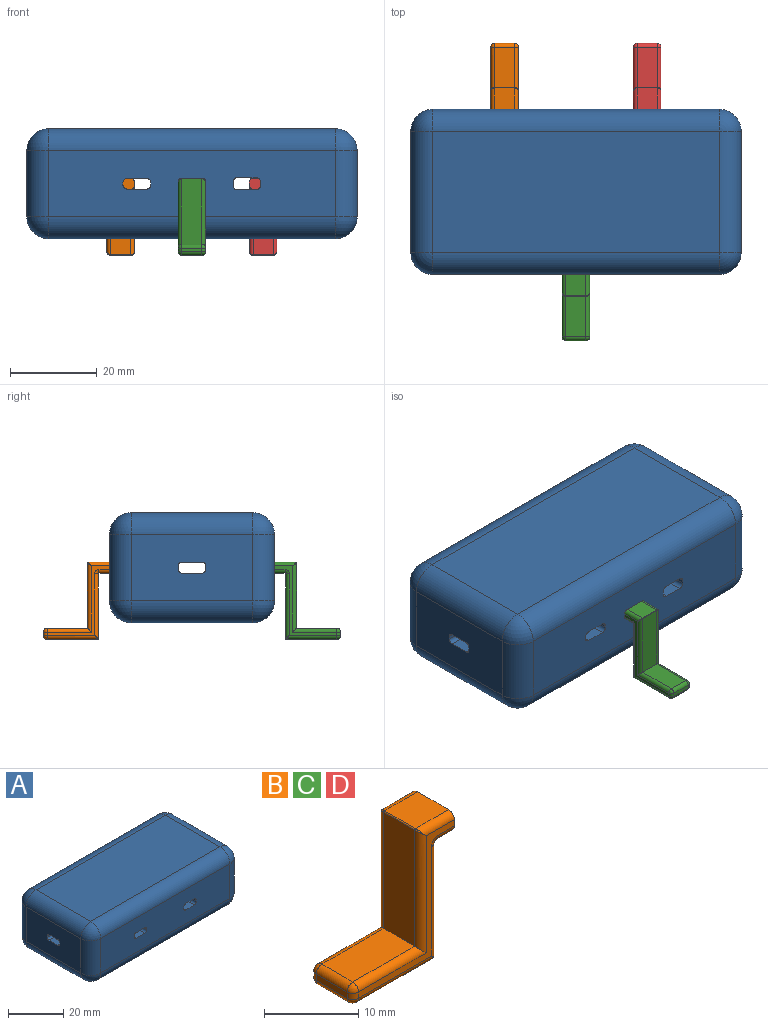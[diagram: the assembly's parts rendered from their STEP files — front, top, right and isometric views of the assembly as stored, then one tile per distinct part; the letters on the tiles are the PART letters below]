
ASSEMBLY  parts=4 mates=1
PART A: 70 faces, bbox 76.2x38.1x25.4 mm
  f0: plane 27.94x15.24mm, normal (1,0,0), area 410.4mm2, adj f21,f30,f31,f35,f62,f63,f64,f65
  f1: plane 27.94x15.24mm, normal (-1,0,0), area 410.4mm2, adj f16,f19,f23,f24,f52,f53,f54,f55
  f2: plane 15.88x0.41mm, normal (1,0,0), area 6.5mm2, adj f9,f12,f37,f60
  f3: cylinder r=1.02mm len=16.48mm, axis (0,1,0), area 25.7mm2, adj f4,f13,f36,f54,f61
  f4: plane 16.48x4.44mm, normal (0,0,-1), area 73.2mm2, adj f3,f5,f13,f54
  f5: cylinder r=1.02mm len=16.48mm, axis (0,1,0), area 25.7mm2, adj f4,f13,f40,f54,f59
  f6: plane 15.88x0.41mm, normal (-1,0,0), area 6.5mm2, adj f7,f12,f39,f58
  f7: cylinder r=1.02mm len=16.48mm, axis (0,1,0), area 25.7mm2, adj f6,f12,f42,f56,f58
  f8: plane 16.48x4.44mm, normal (0,0,1), area 73.2mm2, adj f13,f41,f43,f55
  f9: cylinder r=1.02mm len=16.48mm, axis (0,1,0), area 25.7mm2, adj f2,f12,f42,f56,f60
  f10: plane 15.88x0.77mm, normal (1,0,0), area 12.2mm2, adj f13,f45,f51,f54,f55,f59
  f11: plane 15.88x0.77mm, normal (-1,0,0), area 12.2mm2, adj f13,f47,f49,f63,f64,f68
  f12: plane 66.04x15.24mm, normal (0,-1,0), area 974.7mm2, adj f2,f6,f7,f9,f24,f29,f32,f35
  f13: plane 66.04x15.24mm, normal (0,1,0), area 974.7mm2, adj f3,f4,f5,f8,f10,f11,f16,f20
  f14: plane 66.04x27.94mm, normal (0,0,1), area 1845.2mm2, adj f19,f20,f29,f30
  f15: plane 66.04x27.94mm, normal (0,0,-1), area 1845.2mm2, adj f22,f23,f31,f32
  f16: cylinder r=5.08mm len=15.24mm, axis (0,0,1), area 121.6mm2, adj f1,f13,f17,f18
  f17: sphere r=5.08mm, area 40.5mm2, adj f16,f19,f20
  f18: sphere r=5.08mm, area 40.5mm2, adj f16,f22,f23
  f19: cylinder r=5.08mm len=27.94mm, axis (0,1,0), area 223mm2, adj f1,f14,f17,f25
  f20: cylinder r=5.08mm len=66.04mm, axis (1,0,0), area 527mm2, adj f13,f14,f17,f26
  f21: cylinder r=5.08mm len=15.24mm, axis (0,0,-1), area 121.6mm2, adj f0,f13,f26,f27
  f22: cylinder r=5.08mm len=66.04mm, axis (-1,0,0), area 527mm2, adj f13,f15,f18,f27
  f23: cylinder r=5.08mm len=27.94mm, axis (0,-1,0), area 223mm2, adj f1,f15,f18,f28
  f24: cylinder r=5.08mm len=15.24mm, axis (0,0,-1), area 121.6mm2, adj f1,f12,f25,f28
  f25: sphere r=5.08mm, area 40.5mm2, adj f19,f24,f29
  f26: sphere r=5.08mm, area 40.5mm2, adj f20,f21,f30
  f27: sphere r=5.08mm, area 40.5mm2, adj f21,f22,f31
  f28: sphere r=5.08mm, area 40.5mm2, adj f23,f24,f32
  f29: cylinder r=5.08mm len=66.04mm, axis (-1,0,0), area 527mm2, adj f12,f14,f25,f33
  f30: cylinder r=5.08mm len=27.94mm, axis (0,-1,0), area 223mm2, adj f0,f14,f26,f33
  f31: cylinder r=5.08mm len=27.94mm, axis (0,1,0), area 223mm2, adj f0,f15,f27,f34
  f32: cylinder r=5.08mm len=66.04mm, axis (1,0,0), area 527mm2, adj f12,f15,f28,f34
  f33: sphere r=5.08mm, area 40.5mm2, adj f29,f30,f35
  f34: sphere r=5.08mm, area 40.5mm2, adj f31,f32,f35
  f35: cylinder r=5.08mm len=15.24mm, axis (0,0,1), area 121.6mm2, adj f0,f12,f33,f34
  f36: plane 15.88x0.41mm, normal (1,0,0), area 6.5mm2, adj f3,f13,f43,f61
  f37: cylinder r=1.02mm len=16.48mm, axis (0,1,0), area 25.7mm2, adj f2,f12,f38,f52,f60
  f38: plane 16.48x4.44mm, normal (0,0,-1), area 73.2mm2, adj f12,f37,f39,f52
  f39: cylinder r=1.02mm len=16.48mm, axis (0,1,0), area 25.7mm2, adj f6,f12,f38,f52,f58
  f40: plane 15.88x0.41mm, normal (-1,0,0), area 6.5mm2, adj f5,f13,f41,f59
  f41: cylinder r=1.02mm len=16.48mm, axis (0,1,0), area 25.7mm2, adj f8,f13,f40,f55,f59
  f42: plane 16.48x4.44mm, normal (0,0,1), area 73.2mm2, adj f7,f9,f12,f56
  f43: cylinder r=1.02mm len=16.48mm, axis (0,1,0), area 25.7mm2, adj f8,f13,f36,f55,f61
  f44: plane 15.88x0.77mm, normal (1,0,0), area 12.2mm2, adj f12,f45,f51,f52,f56,f58
  f45: cylinder r=1.02mm len=38.1mm, axis (0,1,0), area 54.5mm2, adj f10,f12,f13,f44,f46,f52,f53,f54
  f46: plane 38.1x4.3mm, normal (0,0,-1), area 163.9mm2, adj f12,f13,f45,f47
  f47: cylinder r=1.02mm len=38.1mm, axis (0,1,0), area 54.5mm2, adj f11,f12,f13,f46,f48,f62,f64,f65
  f48: plane 15.88x0.77mm, normal (-1,0,0), area 12.2mm2, adj f12,f47,f49,f65,f66,f69
  f49: cylinder r=1.02mm len=38.1mm, axis (0,1,0), area 54.5mm2, adj f11,f12,f13,f48,f50,f67,f68,f69
  f50: plane 38.1x4.3mm, normal (0,0,1), area 163.9mm2, adj f12,f13,f49,f51
  f51: cylinder r=1.02mm len=38.1mm, axis (0,1,0), area 54.5mm2, adj f10,f12,f13,f44,f50,f55,f56,f57
  f52: cylinder r=0.89mm len=48.09mm, axis (1,0,0), area 60.4mm2, adj f1,f37,f38,f39,f44,f45,f53,f58
  f53: plane 48.09x4.57mm, normal (0,0,-1), area 219.9mm2, adj f1,f45,f52,f54
  f54: cylinder r=0.89mm len=48.09mm, axis (1,0,0), area 60.4mm2, adj f1,f3,f4,f5,f10,f45,f53,f59
  f55: cylinder r=0.89mm len=48.09mm, axis (1,0,0), area 60.4mm2, adj f1,f8,f10,f41,f43,f51,f57,f59
  f56: cylinder r=0.89mm len=48.09mm, axis (1,0,0), area 60.4mm2, adj f1,f7,f9,f42,f44,f51,f57,f58
  f57: plane 48.09x4.57mm, normal (0,0,1), area 219.9mm2, adj f1,f51,f55,f56
  f58: plane 18.95x0.76mm, normal (0,1,0), area 14.4mm2, adj f6,f7,f39,f44,f52,f56
  f59: plane 18.95x0.76mm, normal (0,-1,0), area 14.4mm2, adj f5,f10,f40,f41,f54,f55
  f60: plane 22.18x0.76mm, normal (0,1,0), area 16.9mm2, adj f1,f2,f9,f37,f52,f56
  f61: plane 22.18x0.76mm, normal (0,-1,0), area 16.9mm2, adj f1,f3,f36,f43,f54,f55
  f62: plane 22.81x4.57mm, normal (0,0,-1), area 104.3mm2, adj f0,f47,f64,f65
  f63: plane 22.29x0.76mm, normal (0,-1,0), area 17mm2, adj f0,f11,f64,f68
  f64: cylinder r=0.89mm len=22.81mm, axis (1,0,0), area 31.5mm2, adj f0,f11,f47,f62,f63
  f65: cylinder r=0.89mm len=22.81mm, axis (1,0,0), area 31.5mm2, adj f0,f47,f48,f62,f66
  f66: plane 22.29x0.76mm, normal (0,1,0), area 17mm2, adj f0,f48,f65,f69
  f67: plane 22.81x4.57mm, normal (0,0,1), area 104.3mm2, adj f0,f49,f68,f69
  f68: cylinder r=0.89mm len=22.81mm, axis (1,0,0), area 31.5mm2, adj f0,f11,f49,f63,f67
  f69: cylinder r=0.89mm len=22.81mm, axis (1,0,0), area 31.5mm2, adj f0,f48,f49,f66,f67
PART B: 39 faces, bbox 15.2x6.4x17.8 mm
  f0: plane 4.95x4.63mm, normal (0,0,1), area 22.9mm2, adj f1,f10,f13,f16
  f1: cylinder r=0.13mm len=4.63mm, axis (0,1,0), area 0.9mm2, adj f0,f2,f14,f19
  f2: plane 15.11x4.63mm, normal (-1,0,0), area 70mm2, adj f1,f3,f17,f22
  f3: plane 9.3x4.63mm, normal (0,0,1), area 43.1mm2, adj f2,f20,f26,f27
  f4: plane 4.63x0.82mm, normal (-1,0,0), area 3.8mm2, adj f27,f28,f34,f35
  f5: plane 11.71x4.63mm, normal (0,0,-1), area 54.3mm2, adj f6,f29,f35,f38
  f6: cylinder r=0.13mm len=4.63mm, axis (0,1,0), area 0.9mm2, adj f5,f7,f24,f36
  f7: plane 14.99x4.63mm, normal (1,0,0), area 69.4mm2, adj f6,f8,f21,f33
  f8: cylinder r=0.13mm len=4.63mm, axis (0,1,0), area 0.9mm2, adj f7,f9,f18,f30
  f9: plane 4.63x2.41mm, normal (0,0,-1), area 11.2mm2, adj f8,f10,f15,f25
  f10: plane 6.35x2.54mm, normal (1,0,0), area 15.5mm2, adj f0,f9,f11,f12,f13,f15,f16,f25
  f11: plane 16.06x14.38mm, normal (0,-1,0), area 24.6mm2, adj f10,f13,f15,f17,f18,f20,f21,f28
  f12: plane 16.06x14.38mm, normal (0,1,0), area 24.6mm2, adj f10,f16,f22,f25,f26,f30,f33,f34
  f13: cylinder r=0.86mm len=4.95mm, axis (1,0,0), area 6.3mm2, adj f0,f10,f11,f14
  f14: bspline ~0.99x0.86mm, area 0.2mm2, adj f1,f13,f17
  f15: cylinder r=0.86mm len=2.41mm, axis (-1,0,0), area 3.3mm2, adj f9,f10,f11,f18
  f16: cylinder r=0.86mm len=4.95mm, axis (-1,0,0), area 6.3mm2, adj f0,f10,f12,f19
  f17: cylinder r=0.86mm len=15.97mm, axis (0,0,1), area 20.4mm2, adj f2,f11,f14,f20
  f18: torus R=0.99mm, axis (0,-1,0), area 0.9mm2, adj f8,f11,f15,f21
  f19: bspline ~0.99x0.86mm, area 0.2mm2, adj f1,f16,f22
  f20: cylinder r=0.86mm len=10.16mm, axis (1,0,0), area 13mm2, adj f3,f11,f17,f23
  f21: cylinder r=0.86mm len=14.99mm, axis (0,0,-1), area 19.9mm2, adj f7,f11,f18,f24
  f22: cylinder r=0.86mm len=15.97mm, axis (0,0,-1), area 20.4mm2, adj f2,f12,f19,f26
  f23: sphere r=0.86mm, area 1.2mm2, adj f20,f27,f28
  f24: bspline ~0.99x0.86mm, area 0.2mm2, adj f6,f21,f29
  f25: cylinder r=0.86mm len=2.41mm, axis (1,0,0), area 3.3mm2, adj f9,f10,f12,f30
  f26: cylinder r=0.86mm len=10.16mm, axis (-1,0,0), area 13mm2, adj f3,f12,f22,f31
  f27: cylinder r=0.86mm len=4.63mm, axis (0,1,0), area 6.2mm2, adj f3,f4,f23,f31
  f28: cylinder r=0.86mm len=0.86mm, axis (0,0,1), area 1.1mm2, adj f4,f11,f23,f32
  f29: cylinder r=0.86mm len=11.71mm, axis (-1,0,0), area 15.4mm2, adj f5,f11,f24,f32
  f30: torus R=0.99mm, axis (0,-1,0), area 0.9mm2, adj f8,f12,f25,f33
  f31: sphere r=0.86mm, area 1.2mm2, adj f26,f27,f34
  f32: sphere r=0.86mm, area 1.2mm2, adj f28,f29,f35
  f33: cylinder r=0.86mm len=14.99mm, axis (0,0,1), area 19.9mm2, adj f7,f12,f30,f36
  f34: cylinder r=0.86mm len=0.86mm, axis (0,0,-1), area 1.1mm2, adj f4,f12,f31,f37
  f35: cylinder r=0.86mm len=4.63mm, axis (0,-1,0), area 6.2mm2, adj f4,f5,f32,f37
  f36: bspline ~0.99x0.86mm, area 0.2mm2, adj f6,f33,f38
  f37: sphere r=0.86mm, area 1.2mm2, adj f34,f35,f38
  f38: cylinder r=0.86mm len=11.71mm, axis (1,0,0), area 15.4mm2, adj f5,f12,f36,f37
PART C: same geometry as B
PART D: same geometry as B
PLACE A at identity fixed
PLACE B rot(axis=(0,0,-1),90deg) t=(-16.46,19.05,-1.27)mm
PLACE C rot(axis=(0,0,1),90deg) t=(-0.02,-19.05,-1.27)mm
PLACE D rot(axis=(0,0,-1),90deg) t=(16.41,19.05,-1.27)mm
MATE fastened A.f12 <-> C.f10  axis (0,-1,0) through (-0.02,-19.05,0)mm
